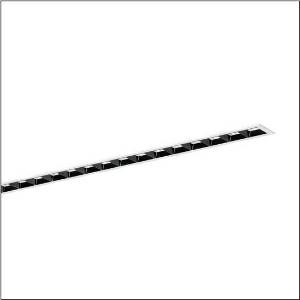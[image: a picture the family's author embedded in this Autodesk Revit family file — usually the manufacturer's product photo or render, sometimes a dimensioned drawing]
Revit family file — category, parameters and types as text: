
# Revit family: silica_r__21_51mx12da34wb_5af2
name_source: partatom
category: Lighting Fixtures
units: mm (PartAtom-declared; Revit-internal decimal feet)

## family parameters
Cut with Voids When Loaded = No
Host = Face
Light Source = No
Part Type = Normal
Room Calculation Point = No
Round Connector Dimension = Use Diameter
Shared = No

## types (1)
- --- (1 x LED, 4320 lm, 27.4 W, 3000K)
    Apparent Load = 27 VA
    CIE Flux Codes = 86 100 100 100 100
    Color Rendering = 80
    Color Temperature = 3000K
    Default Elevation = 1800 mm
    Description = Silica® 21, office luminaire, primary light control with darklight reflector, of PMMA, black, CAT 2 (L<= 3000cd/m²), light emission: direct distribution, primary light characteristic: symmetric, installation type: recessed, LED, rated luminous flux: 4.320lm, luminous efficacy: 158lm/W, light colour: 830, colour temperature: 3000K, with terminal, 3+2-pole, max. 2.5mm², mains connection: 220..240V, AC, 50/60Hz, rated input power: 27.4W, luminaire housing, of aluminium, traffic white (RAL 9016), length: 1.228mm, width: 79mm, height: 53mm, protection rating (complete): IP20, insulation class (complete): insulation class I (protective earthing), certification: CE, permissible operating ambient temperature: 0..+35°C, standard: EN 50419, packaging unit: 1 piece
    Height = 0 mm  [stored 0 ft]
    Lamp = 1 x LED
    Lamp Light Flux = 4320 lm
    Lamp Power = 27.4 W
    Lamp count = 1
    Length = 1227 mm
    Luminous efficacy = 158 lm/W
    Manufacturer = Siteco
    ModVariant = No
    Model = 51MX12DA34WB
    Mounting Place = Ceiling
    Mounting Type = Recessed
    Number of Poles = 1
    OnlyDefault = Yes
    Power Factor = 1
    Product Name = Silica® 21
    Product group = office luminaire | ceiling recessed
    ProductGroupID = 400
    Protection Class = Protection class I
    Protection Degree = IP 20
    RLX_Detail_Level = 1
    RlxData = <blob elided: 38525 chars, md5=e4f6c77b>
    Socket = socket
    Standby Power = 0 W
    System Light Flux = 4320 lm
    System Power = 27 W
    Type Comments = factory setting: luminous flux: 100 % | dim-lin: 254 | 392 mA
    Type Image = l_1251632.jpg
    URL = http://relux.com
    VarID = @adj_034193
    Voltage = 0 V
    Weight = 0.00 kg
    Width = 79 mm

note: [stored X ft] marks values corroborated as IEEE doubles in the binary element streams (Revit-internal decimal feet)

## geometry (parser evidence)
native form markers: Blend x4, Sweep x10
no freeform markers — native parametric forms only
